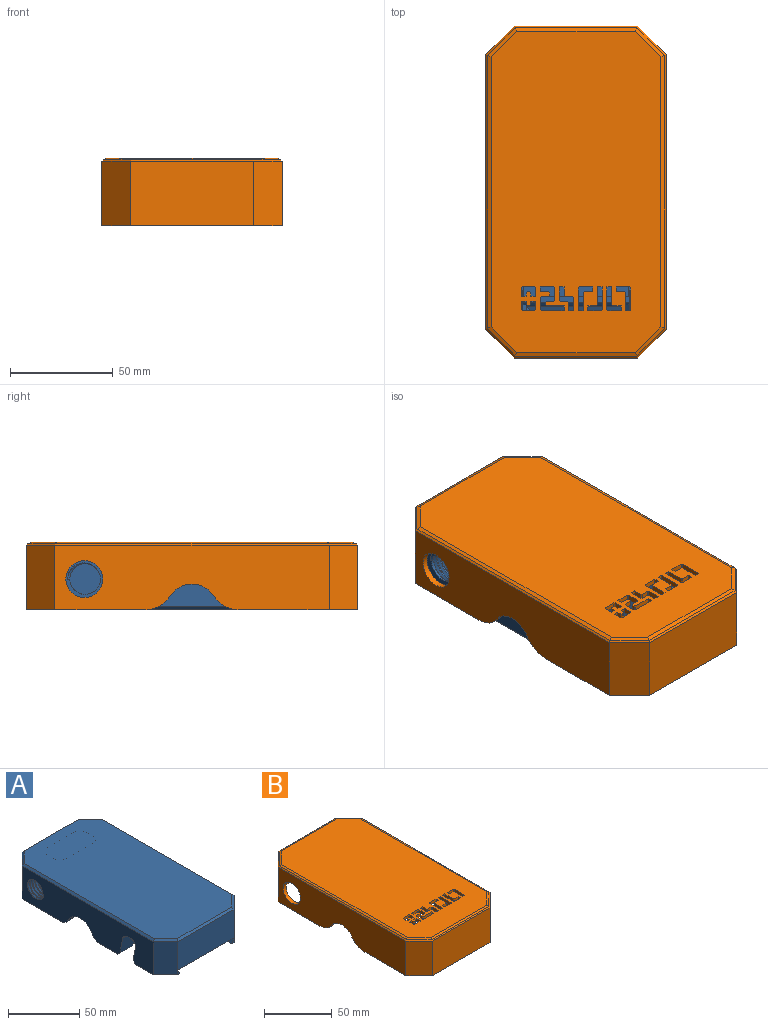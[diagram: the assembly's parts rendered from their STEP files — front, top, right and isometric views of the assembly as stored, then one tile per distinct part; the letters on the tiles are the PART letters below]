
ASSEMBLY  parts=2 mates=3
PART A: 142 faces, bbox 82.7x155.7x31.4 mm
  f0: plane 30x14mm, normal (0,0,-1), area 348mm2, adj f5,f14,f17,f33,f83
  f1: plane 4x2mm, normal (0,-1,0), area 4mm2, adj f13,f34,f82
  f2: plane 56x24.4mm, normal (0,-1,0), area 1366.4mm2, adj f33,f34,f84,f109
  f3: plane 25.83x20.32mm, normal (0,0,-1), area 273.5mm2, adj f4,f14,f15,f26,f67,f71,f85
  f4: plane 14x2.41mm, normal (0,-0.63,-0.77), area 42.1mm2, adj f3,f14,f51,f85
  f5: plane 14x2.94mm, normal (0,0.77,-0.63), area 50.5mm2, adj f0,f14,f52,f83
  f6: plane 53.34x25.97mm, normal (0,0,-1), area 726.6mm2, adj f7,f16,f21,f22,f23,f31,f35,f66
  f7: plane 131.67x29.07mm, normal (-1,0,0), area 3016.5mm2, adj f6,f10,f13,f31,f34,f37,f39,f40
  f8: cone r=37.8mm half-angle=45deg, axis (0,0,-1), area 57mm2, adj f9,f12,f23,f72
  f9: plane 53.34x25.97mm, normal (0,0,-1), area 726.6mm2, adj f8,f14,f16,f21,f23,f24,f32,f68
  f10: plane 25.83x20.32mm, normal (0,0,-1), area 273.5mm2, adj f7,f11,f26,f62,f65,f69,f87
  f11: cone r=37.8mm half-angle=45deg, axis (0,0,-1), area 57mm2, adj f10,f26,f36,f69
  f12: cone r=32.8mm half-angle=22.5deg, axis (0,0,-1), area 726.8mm2, adj f8,f19,f23,f35,f63,f64,f70,f72
  f13: plane 30x14mm, normal (0,0,-1), area 348mm2, adj f1,f7,f34,f61,f82
  f14: plane 131.65x29.05mm, normal (1,0,0), area 3016.5mm2, adj f0,f3,f4,f5,f9,f32,f33,f44
  f15: cone r=37.8mm half-angle=45deg, axis (0,0,-1), area 57mm2, adj f3,f26,f36,f71
  f16: plane 56x28.4mm, normal (0,1,0), area 1418.1mm2, adj f6,f9,f31,f32,f77,f78,f79,f80
  f17: plane 4x2mm, normal (0,-1,0), area 4mm2, adj f0,f33,f83
  f18: plane 151.8x76.8mm, normal (0,0,1), area 11413.5mm2, adj f105,f106,f107,f108,f109,f110,f111,f112
  f19: cylinder r=32.8mm len=65.6mm, axis (0,0,-1), area 2267mm2, adj f12,f30,f36,f63,f64
  f20: plane 60.6x60.6mm, normal (0,0,-1), area 2884.3mm2, adj f30
  f21: plane 51x14.5mm, normal (0,-1,0), area 567.2mm2, adj f6,f9,f22,f24,f25,f77,f78,f79
  f22: plane 31x14.5mm, normal (1,0,0), area 449.5mm2, adj f6,f21,f23,f25
  f23: plane 51.2x14.7mm, normal (0,1,0), area 662.1mm2, adj f6,f8,f9,f12,f22,f24,f25,f35
  f24: plane 31x14.5mm, normal (-1,0,0), area 449.5mm2, adj f9,f21,f23,f25
  f25: plane 51x31mm, normal (0,0,-1), area 458mm2, adj f21,f22,f23,f24,f113,f114,f115,f116
  f26: plane 56.2x27.2mm, normal (0,-1,0), area 1323.1mm2, adj f3,f10,f11,f15,f27,f29,f36,f85
  f27: plane 23x23mm, normal (1,0,0), area 332.7mm2, adj f26,f28,f54,f55,f56,f57,f58,f84
  f28: plane 51.5x23mm, normal (0,1,0), area 1184.5mm2, adj f27,f29,f84,f104
  f29: plane 23x23mm, normal (-1,0,0), area 332.7mm2, adj f26,f28,f51,f52,f53,f59,f60,f84
  f30: cone r=32.8mm half-angle=45deg, axis (0,0,-1), area 700.9mm2, adj f19,f20
  f31: plane 28.4x12mm, normal (-0.71,0.71,0), area 482mm2, adj f6,f7,f16,f106
  f32: plane 28.4x12mm, normal (0.71,0.71,0), area 482mm2, adj f9,f14,f16,f110
  f33: plane 28.4x12mm, normal (0.71,-0.71,0), area 482mm2, adj f0,f2,f14,f17,f111
  f34: plane 28.4x12mm, normal (-0.71,-0.71,0), area 482mm2, adj f1,f2,f7,f13,f107
  f35: cone r=37.8mm half-angle=45deg, axis (0,0,-1), area 57mm2, adj f6,f12,f23,f70
  f36: cone r=32.8mm half-angle=22.5deg, axis (0,0,-1), area 726.8mm2, adj f11,f15,f19,f26,f63,f64,f69,f71
  f37: cylinder r=7.5mm len=15mm, axis (-1,0,0), area 114.4mm2, adj f7,f38,f39,f40,f42,f43
  f38: plane 15x15mm, normal (-1,0,0), area 176.7mm2, adj f37,f41
  f39: plane 1x1mm, normal (0,0,-1), area 0.5mm2, adj f7,f37,f43
  f40: bspline ~19.63x17mm, area 270.1mm2, adj f7,f37,f42,f43
  f41: cylinder r=7.5mm len=13.59mm, axis (1,0,0), area 9.4mm2, adj f38,f42,f43
  f42: plane 2x1mm, normal (0,0,1), area 1mm2, adj f37,f40,f41,f43
  f43: bspline ~19.63x17mm, area 284.7mm2, adj f37,f39,f40,f41,f42
  f44: cylinder r=7.5mm len=15mm, axis (1,0,0), area 114.4mm2, adj f14,f45,f47,f48,f49,f50
  f45: plane 15x15mm, normal (1,0,0), area 176.7mm2, adj f44,f46
  f46: cylinder r=7.5mm len=13.59mm, axis (-1,0,0), area 9.4mm2, adj f45,f48,f49
  f47: plane 1x1mm, normal (0,0,-1), area 0.5mm2, adj f14,f44,f49
  f48: plane 2x1mm, normal (0,0,1), area 1mm2, adj f44,f46,f49,f50
  f49: bspline ~19.63x17mm, area 284.7mm2, adj f44,f46,f47,f48,f50
  f50: bspline ~19.63x17mm, area 270.1mm2, adj f14,f44,f48,f49
  f51: plane 14.25x14mm, normal (0,-0.98,-0.2), area 199.9mm2, adj f4,f14,f29,f59,f85,f86
  f52: plane 14.25x11.08mm, normal (0,0.98,0.2), area 158.8mm2, adj f5,f14,f29,f60,f83,f84
  f53: plane 14.25x2.8mm, normal (0,0,-1), area 39.9mm2, adj f14,f29,f59,f60
  f54: plane 14.25x2.8mm, normal (0,0,-1), area 39.9mm2, adj f7,f27,f57,f58
  f55: plane 14.25x14mm, normal (0,-0.98,-0.2), area 199.9mm2, adj f7,f27,f57,f62,f87,f88
  f56: plane 14.25x11.08mm, normal (0,0.98,0.2), area 158.8mm2, adj f7,f27,f58,f61,f82,f84
  f57: cylinder r=5mm len=14.25mm, axis (-1,0,0), area 97.9mm2, adj f7,f27,f54,f55
  f58: cylinder r=5mm len=14.25mm, axis (-1,0,0), area 126mm2, adj f7,f27,f54,f56
  f59: cylinder r=5mm len=14.25mm, axis (-1,0,0), area 97.9mm2, adj f14,f29,f51,f53
  f60: cylinder r=5mm len=14.25mm, axis (-1,0,0), area 126mm2, adj f14,f29,f52,f53
  f61: plane 14x2.94mm, normal (0,0.77,-0.63), area 50.5mm2, adj f7,f13,f56,f82
  f62: plane 14x2.41mm, normal (0,-0.63,-0.77), area 42.1mm2, adj f7,f10,f55,f87
  f63: cylinder r=12.5mm len=22.56mm, axis (-1,0,0), area 220.3mm2, adj f7,f12,f19,f36,f69,f70,f74,f75
  f64: cylinder r=12.5mm len=22.56mm, axis (-1,0,0), area 220.2mm2, adj f12,f14,f19,f36,f71,f72,f73,f76
  f65: plane 5.16x2.75mm, normal (0,0.6,-0.8), area 16.8mm2, adj f7,f10,f69,f74
  f66: plane 5.16x2.75mm, normal (0,-0.6,-0.8), area 16.8mm2, adj f6,f7,f70,f75
  f67: plane 5.16x2.75mm, normal (0,0.6,-0.8), area 16.8mm2, adj f3,f14,f71,f73
  f68: plane 5.16x2.75mm, normal (0,-0.6,-0.8), area 16.8mm2, adj f9,f14,f72,f76
  f69: bspline ~9.3x8.08mm, area 25.5mm2, adj f10,f11,f36,f63,f65,f74
  f70: bspline ~9.3x8.08mm, area 25.5mm2, adj f6,f12,f35,f63,f66,f75
  f71: bspline ~9.3x8.08mm, area 25.5mm2, adj f3,f15,f36,f64,f67,f73
  f72: bspline ~9.3x8.08mm, area 25.5mm2, adj f8,f9,f12,f64,f68,f76
  f73: plane 6.37x3.46mm, normal (0,0.77,-0.64), area 23.8mm2, adj f14,f64,f67,f71
  f74: plane 6.37x3.46mm, normal (0,0.77,-0.64), area 23.8mm2, adj f7,f63,f65,f69
  f75: plane 6.37x3.46mm, normal (0,-0.77,-0.64), area 23.8mm2, adj f7,f63,f66,f70
  f76: plane 6.37x3.46mm, normal (0,-0.77,-0.64), area 23.8mm2, adj f14,f64,f68,f72
  f77: cylinder r=10mm len=17.38mm, axis (0,1,0), area 84.3mm2, adj f16,f21,f80,f81
  f78: plane 4x2.7mm, normal (0.58,0,-0.82), area 13.2mm2, adj f6,f16,f21,f80
  f79: plane 4x2.7mm, normal (-0.58,0,-0.82), area 13.2mm2, adj f9,f16,f21,f81
  f80: plane 4x3.04mm, normal (0.74,0,-0.67), area 16.4mm2, adj f16,f21,f77,f78
  f81: plane 4x3.04mm, normal (-0.74,0,-0.67), area 16.4mm2, adj f16,f21,f77,f79
  f82: plane 32.41x4mm, normal (0.89,0,0.45), area 140.9mm2, adj f1,f13,f56,f61,f84
  f83: plane 32.41x4mm, normal (-0.89,0,0.45), area 140.9mm2, adj f0,f5,f17,f52,f84
  f84: plane 56x32.2mm, normal (0,0,-1), area 443.4mm2, adj f2,f27,f28,f29,f52,f56,f82,f83
  f85: plane 4.8x4mm, normal (-0.89,0,0.45), area 17.4mm2, adj f3,f4,f26,f51,f86
  f86: plane 4.8x2.25mm, normal (0,0,-1), area 10.8mm2, adj f26,f29,f51,f85
  f87: plane 4.8x4mm, normal (0.89,0,0.45), area 17.4mm2, adj f10,f26,f55,f62,f88
  f88: plane 4.8x2.25mm, normal (0,0,-1), area 10.8mm2, adj f26,f27,f55,f87
  f89: plane 43x12mm, normal (0,0,-1), area 516mm2, adj f90,f91,f92,f93
  f90: plane 48.12x2.56mm, normal (0,0.38,-0.92), area 126.3mm2, adj f89,f92,f93,f94
  f91: plane 48.12x2.56mm, normal (0,-0.38,-0.92), area 126.3mm2, adj f89,f92,f93,f95
  f92: plane 17.12x2.56mm, normal (0.38,0,-0.92), area 40.4mm2, adj f89,f90,f91,f96
  f93: plane 17.12x2.56mm, normal (-0.38,0,-0.92), area 40.4mm2, adj f89,f90,f91,f97
  f94: plane 49.88x0.88mm, normal (0,0.71,-0.71), area 60.9mm2, adj f90,f96,f97,f98
  f95: plane 49.88x0.88mm, normal (0,-0.71,-0.71), area 60.9mm2, adj f91,f96,f97,f99
  f96: plane 19.76x1.94mm, normal (0.71,0,-0.71), area 51.3mm2, adj f92,f94,f95,f98,f99,f103
  f97: plane 19.76x1.94mm, normal (-0.71,0,-0.71), area 51.3mm2, adj f93,f94,f95,f98,f99,f102
  f98: plane 52x2.56mm, normal (0,0.92,-0.38), area 142.9mm2, adj f94,f96,f97,f101,f102,f103
  f99: plane 52x2.56mm, normal (0,-0.92,-0.38), area 142.9mm2, adj f95,f96,f97,f100,f102,f103
  f100: plane 52x18.5mm, normal (0,-1,0), area 962mm2, adj f84,f99,f102,f103
  f101: plane 52x18.5mm, normal (0,1,0), area 962mm2, adj f84,f98,f102,f103
  f102: plane 21x20mm, normal (-1,0,0), area 419.1mm2, adj f84,f97,f98,f99,f100,f101
  f103: plane 21x20mm, normal (1,0,0), area 419.1mm2, adj f84,f96,f98,f99,f100,f101
  f104: plane 51.5x23mm, normal (0,0,-1), area 1184.5mm2, adj f26,f27,f28,f29
  f105: plane 131x1.6mm, normal (-0.71,0,0.71), area 294.9mm2, adj f7,f18,f106,f107
  f106: plane 12.66x12.66mm, normal (-0.5,0.5,0.71), area 36.9mm2, adj f18,f31,f105,f108
  f107: plane 12.66x12.66mm, normal (-0.5,-0.5,0.71), area 36.9mm2, adj f18,f34,f105,f109
  f108: plane 56x1.6mm, normal (0,0.71,0.71), area 125.2mm2, adj f16,f18,f106,f110
  f109: plane 56x1.6mm, normal (0,-0.71,0.71), area 125.2mm2, adj f2,f18,f107,f111
  f110: plane 12.66x12.66mm, normal (0.5,0.5,0.71), area 36.9mm2, adj f18,f32,f108,f112
  f111: plane 12.66x12.66mm, normal (0.5,-0.5,0.71), area 36.9mm2, adj f18,f33,f109,f112
  f112: plane 131x1.6mm, normal (0.71,0,0.71), area 294.9mm2, adj f14,f18,f110,f111
  f113: plane 43x9.68mm, normal (0,1,0), area 416.3mm2, adj f25,f130,f140,f141
  f114: plane 23x9.68mm, normal (1,0,0), area 222.7mm2, adj f25,f135,f139,f140
  f115: plane 43x9.68mm, normal (0,-1,0), area 416.3mm2, adj f25,f137,f138,f139
  f116: plane 23x9.68mm, normal (-1,0,0), area 222.7mm2, adj f25,f134,f138,f141
  f117: plane 39x19mm, normal (0,0,-1), area 706.2mm2, adj f118,f119,f120,f121,f122,f123,f124,f125
  f118: plane 30.7x1.36mm, normal (0,0.71,-0.71), area 56.4mm2, adj f117,f126,f127,f130
  f119: plane 10.7x1.36mm, normal (0.71,0,-0.71), area 18mm2, adj f117,f131,f132,f135
  f120: plane 10.7x1.36mm, normal (-0.71,0,-0.71), area 18mm2, adj f117,f128,f129,f134
  f121: plane 30.7x1.36mm, normal (0,-0.71,-0.71), area 56.4mm2, adj f117,f133,f136,f137
  f122: plane 5.21x5.21mm, normal (-0.41,-0.41,-0.82), area 14.5mm2, adj f117,f128,f133,f134,f137,f138
  f123: plane 5.21x5.21mm, normal (0.41,-0.41,-0.82), area 14.5mm2, adj f117,f132,f135,f136,f137,f139
  f124: plane 5.21x5.21mm, normal (0.41,0.41,-0.82), area 14.5mm2, adj f117,f127,f130,f131,f135,f140
  f125: plane 5.21x5.21mm, normal (-0.41,0.41,-0.82), area 14.5mm2, adj f117,f126,f129,f130,f134,f141
  f126: plane 6.07x3.17mm, normal (-0.21,0.58,-0.79), area 11.4mm2, adj f117,f118,f125,f130
  f127: plane 6.07x3.17mm, normal (0.21,0.58,-0.79), area 11.4mm2, adj f117,f118,f124,f130
  f128: plane 6.07x3.17mm, normal (-0.58,-0.21,-0.79), area 11.4mm2, adj f117,f120,f122,f134
  f129: plane 6.07x3.17mm, normal (-0.58,0.21,-0.79), area 11.4mm2, adj f117,f120,f125,f134
  f130: plane 43.81x3.96mm, normal (0,0.92,-0.38), area 168.5mm2, adj f113,f118,f124,f125,f126,f127,f140,f141
  f131: plane 6.07x3.17mm, normal (0.58,0.21,-0.79), area 11.4mm2, adj f117,f119,f124,f135
  f132: plane 6.07x3.17mm, normal (0.58,-0.21,-0.79), area 11.4mm2, adj f117,f119,f123,f135
  f133: plane 6.07x3.17mm, normal (-0.21,-0.58,-0.79), area 11.4mm2, adj f117,f121,f122,f137
  f134: plane 23.81x3.96mm, normal (-0.92,0,-0.38), area 82.8mm2, adj f116,f120,f122,f125,f128,f129,f138,f141
  f135: plane 23.81x3.96mm, normal (0.92,0,-0.38), area 82.8mm2, adj f114,f119,f123,f124,f131,f132,f139,f140
  f136: plane 6.07x3.17mm, normal (0.21,-0.58,-0.79), area 11.4mm2, adj f117,f121,f123,f137
  f137: plane 43.81x3.96mm, normal (0,-0.92,-0.38), area 168.5mm2, adj f115,f121,f122,f123,f133,f136,f138,f139
  f138: plane 10.66x1mm, normal (-0.71,-0.71,0), area 14.5mm2, adj f25,f115,f116,f122,f134,f137
  f139: plane 10.66x1mm, normal (0.71,-0.71,0), area 14.5mm2, adj f25,f114,f115,f123,f135,f137
  f140: plane 10.66x1mm, normal (0.71,0.71,0), area 14.5mm2, adj f25,f113,f114,f124,f130,f135
  f141: plane 10.66x1mm, normal (-0.71,0.71,0), area 14.5mm2, adj f25,f113,f116,f125,f130,f134
PART B: 132 faces, bbox 88x161.8x33 mm
  f0: plane 156.6x82.8mm, normal (0,0,1), area 12343mm2, adj f36,f37,f38,f39,f40,f41,f42,f43
  f1: plane 133.8x31.4mm, normal (1,0,0), area 3669.4mm2, adj f2,f6,f17,f18,f20,f22,f24,f25
  f2: plane 88x57.85mm, normal (0,0,-1), area 541.1mm2, adj f1,f3,f5,f7,f9,f10,f12,f13
  f3: plane 133.8x31.4mm, normal (-1,0,0), area 3669.4mm2, adj f2,f6,f16,f19,f21,f23,f26,f27
  f4: plane 60x31.4mm, normal (0,-1,0), area 1884mm2, adj f6,f18,f19,f31
  f5: plane 60x31.4mm, normal (0,1,0), area 1884mm2, adj f2,f16,f17,f32
  f6: plane 88x57.85mm, normal (0,0,-1), area 541.1mm2, adj f1,f3,f4,f7,f8,f9,f14,f15
  f7: plane 131.8x30.4mm, normal (1,0,0), area 3474.8mm2, adj f2,f6,f11,f12,f15,f21,f23,f26
  f8: plane 58x30.4mm, normal (0,1,0), area 1763.2mm2, adj f6,f11,f14,f15
  f9: plane 131.8x30.4mm, normal (-1,0,0), area 3474.8mm2, adj f2,f6,f11,f13,f14,f20,f22,f24
  f10: plane 58x30.4mm, normal (0,-1,0), area 1763.2mm2, adj f2,f11,f12,f13
  f11: plane 155.8x82mm, normal (0,0,-1), area 12175.4mm2, adj f7,f8,f9,f10,f12,f13,f14,f15
  f12: plane 30.4x12mm, normal (0.71,-0.71,0), area 515.9mm2, adj f2,f7,f10,f11
  f13: plane 30.4x12mm, normal (-0.71,-0.71,0), area 515.9mm2, adj f2,f9,f10,f11
  f14: plane 30.4x12mm, normal (-0.71,0.71,0), area 515.9mm2, adj f6,f8,f9,f11
  f15: plane 30.4x12mm, normal (0.71,0.71,0), area 515.9mm2, adj f6,f7,f8,f11
  f16: plane 31.4x14mm, normal (-0.71,0.71,0), area 621.7mm2, adj f2,f3,f5,f30
  f17: plane 31.4x14mm, normal (0.71,0.71,0), area 621.7mm2, adj f1,f2,f5,f34
  f18: plane 31.4x14mm, normal (0.71,-0.71,0), area 621.7mm2, adj f1,f4,f6,f33
  f19: plane 31.4x14mm, normal (-0.71,-0.71,0), area 621.7mm2, adj f3,f4,f6,f29
  f20: cylinder r=9mm len=18mm, axis (-1,0,0), area 169.6mm2, adj f1,f9
  f21: cylinder r=9mm len=18mm, axis (-1,0,0), area 169.6mm2, adj f3,f7
  f22: cylinder r=12.5mm len=20.95mm, axis (1,0,0), area 74.5mm2, adj f1,f9,f24,f25
  f23: cylinder r=12.5mm len=20.95mm, axis (1,0,0), area 74.5mm2, adj f3,f7,f26,f27
  f24: cylinder r=15mm len=12.57mm, axis (1,0,0), area 44.7mm2, adj f1,f6,f9,f22
  f25: cylinder r=15mm len=12.57mm, axis (1,0,0), area 44.7mm2, adj f1,f2,f9,f22
  f26: cylinder r=15mm len=12.57mm, axis (1,0,0), area 44.7mm2, adj f2,f3,f7,f23
  f27: cylinder r=15mm len=12.57mm, axis (1,0,0), area 44.7mm2, adj f3,f6,f7,f23
  f28: plane 133.8x0.89mm, normal (-0.71,0,0.71), area 168.5mm2, adj f3,f29,f30,f36
  f29: plane 14.37x14.37mm, normal (-0.5,-0.5,0.71), area 24.5mm2, adj f19,f28,f31,f37
  f30: plane 14.37x14.37mm, normal (-0.5,0.5,0.71), area 24.5mm2, adj f16,f28,f32,f38
  f31: plane 60x0.89mm, normal (0,-0.71,0.71), area 75.3mm2, adj f4,f29,f33,f39
  f32: plane 60x0.89mm, normal (0,0.71,0.71), area 75.3mm2, adj f5,f30,f34,f40
  f33: plane 14.37x14.37mm, normal (0.5,-0.5,0.71), area 24.5mm2, adj f18,f31,f35,f41
  f34: plane 14.37x14.37mm, normal (0.5,0.5,0.71), area 24.5mm2, adj f17,f32,f35,f42
  f35: plane 133.8x0.89mm, normal (0.71,0,0.71), area 168.5mm2, adj f1,f33,f34,f43
  f36: plane 133.06x1.71mm, normal (-0.38,0,0.92), area 244.6mm2, adj f0,f28,f37,f38
  f37: plane 14.18x14.18mm, normal (-0.27,-0.27,0.92), area 33.9mm2, adj f0,f29,f36,f39
  f38: plane 14.18x14.18mm, normal (-0.27,0.27,0.92), area 33.9mm2, adj f0,f30,f36,f40
  f39: plane 59.26x1.71mm, normal (0,-0.38,0.92), area 108.2mm2, adj f0,f31,f37,f41
  f40: plane 59.26x1.71mm, normal (0,0.38,0.92), area 108.2mm2, adj f0,f32,f38,f42
  f41: plane 14.18x14.18mm, normal (0.27,-0.27,0.92), area 33.9mm2, adj f0,f33,f39,f43
  f42: plane 14.18x14.18mm, normal (0.27,0.27,0.92), area 33.9mm2, adj f0,f34,f40,f43
  f43: plane 133.06x1.71mm, normal (0.38,0,0.92), area 244.6mm2, adj f0,f35,f41,f42
  f44: plane 4.14x2.6mm, normal (0,1,0), area 10.8mm2, adj f0,f11,f45,f125
  f45: plane 2.6x2.32mm, normal (1,0,0), area 6mm2, adj f0,f11,f44,f46
  f46: plane 6.46x2.6mm, normal (0,-1,0), area 16.8mm2, adj f0,f11,f45,f124
  f47: plane 11.1x2.6mm, normal (-1,0,0), area 28.9mm2, adj f0,f11,f48,f124
  f48: plane 2.6x2.32mm, normal (0,1,0), area 6mm2, adj f0,f11,f47,f49
  f49: plane 8.78x2.6mm, normal (1,0,0), area 22.8mm2, adj f0,f11,f48,f125
  f50: plane 11.1x2.6mm, normal (0,1,0), area 28.9mm2, adj f0,f11,f61,f112
  f51: plane 5.96x2.6mm, normal (1,0,0), area 15.5mm2, adj f0,f11,f112,f118
  f52: plane 3.64x2.6mm, normal (0,-1,0), area 9.5mm2, adj f0,f11,f117,f118
  f53: plane 2.6x1.32mm, normal (1,0,0), area 3.4mm2, adj f0,f11,f116,f117
  f54: plane 4.14x2.6mm, normal (0,1,0), area 10.8mm2, adj f0,f11,f55,f116
  f55: plane 2.6x2.32mm, normal (1,0,0), area 6mm2, adj f0,f11,f54,f56
  f56: plane 6.46x2.6mm, normal (0,-1,0), area 16.8mm2, adj f0,f11,f55,f115
  f57: plane 5.96x2.6mm, normal (-1,0,0), area 15.5mm2, adj f0,f11,f115,f119
  f58: plane 3.64x2.6mm, normal (0,1,0), area 9.5mm2, adj f0,f11,f113,f119
  f59: plane 2.6x1.32mm, normal (-1,0,0), area 3.4mm2, adj f0,f11,f113,f114
  f60: plane 8.78x2.6mm, normal (0,-1,0), area 22.8mm2, adj f0,f11,f61,f114
  f61: plane 2.6x2.32mm, normal (-1,0,0), area 6mm2, adj f0,f11,f50,f60
  f62: plane 4.14x2.6mm, normal (-1,0,0), area 10.8mm2, adj f0,f11,f63,f108
  f63: plane 2.6x2.32mm, normal (0,1,0), area 6mm2, adj f0,f11,f62,f64
  f64: plane 2.6x1.82mm, normal (1,0,0), area 4.7mm2, adj f0,f11,f63,f105
  f65: plane 2.6x1.32mm, normal (0,1,0), area 3.4mm2, adj f0,f11,f104,f105
  f66: plane 2.6x1.82mm, normal (-1,0,0), area 4.7mm2, adj f0,f11,f67,f104
  f67: plane 2.6x2.32mm, normal (0,1,0), area 6mm2, adj f0,f11,f66,f68
  f68: plane 4.14x2.6mm, normal (1,0,0), area 10.8mm2, adj f0,f11,f67,f109
  f69: plane 5.96x2.6mm, normal (0,-1,0), area 15.5mm2, adj f0,f11,f108,f109
  f70: plane 4.14x2.6mm, normal (-1,0,0), area 10.8mm2, adj f0,f11,f77,f111
  f71: plane 5.96x2.6mm, normal (0,1,0), area 15.5mm2, adj f0,f11,f110,f111
  f72: plane 4.14x2.6mm, normal (1,0,0), area 10.8mm2, adj f0,f11,f73,f110
  f73: plane 2.6x2.32mm, normal (0,-1,0), area 6mm2, adj f0,f11,f72,f74
  f74: plane 2.6x1.82mm, normal (-1,0,0), area 4.7mm2, adj f0,f11,f73,f106
  f75: plane 2.6x1.32mm, normal (0,-1,0), area 3.4mm2, adj f0,f11,f106,f107
  f76: plane 2.6x1.82mm, normal (1,0,0), area 4.7mm2, adj f0,f11,f77,f107
  f77: plane 2.6x2.32mm, normal (0,-1,0), area 6mm2, adj f0,f11,f70,f76
  f78: plane 8.78x2.6mm, normal (-1,0,0), area 22.8mm2, adj f0,f11,f83,f126
  f79: plane 4.14x2.6mm, normal (0,-1,0), area 10.8mm2, adj f0,f11,f80,f126
  f80: plane 2.6x2.32mm, normal (-1,0,0), area 6mm2, adj f0,f11,f79,f81
  f81: plane 6.46x2.6mm, normal (0,1,0), area 16.8mm2, adj f0,f11,f80,f127
  f82: plane 11.1x2.6mm, normal (1,0,0), area 28.9mm2, adj f0,f11,f83,f127
  f83: plane 2.6x2.32mm, normal (0,-1,0), area 6mm2, adj f0,f11,f78,f82
  f84: plane 6.46x2.6mm, normal (0,1,0), area 16.8mm2, adj f0,f11,f85,f128
  f85: plane 2.6x2.32mm, normal (1,0,0), area 6mm2, adj f0,f11,f84,f86
  f86: plane 4.14x2.6mm, normal (0,-1,0), area 10.8mm2, adj f0,f11,f85,f129
  f87: plane 8.78x2.6mm, normal (1,0,0), area 22.8mm2, adj f0,f11,f88,f129
  f88: plane 2.6x2.32mm, normal (0,-1,0), area 6mm2, adj f0,f11,f87,f89
  f89: plane 11.1x2.6mm, normal (-1,0,0), area 28.9mm2, adj f0,f11,f88,f128
  f90: plane 4.14x2.6mm, normal (0,1,0), area 10.8mm2, adj f0,f11,f95,f131
  f91: plane 8.78x2.6mm, normal (-1,0,0), area 22.8mm2, adj f0,f11,f92,f131
  f92: plane 2.6x2.32mm, normal (0,1,0), area 6mm2, adj f0,f11,f91,f93
  f93: plane 11.1x2.6mm, normal (1,0,0), area 28.9mm2, adj f0,f11,f92,f130
  f94: plane 6.46x2.6mm, normal (0,-1,0), area 16.8mm2, adj f0,f11,f95,f130
  f95: plane 2.6x2.32mm, normal (-1,0,0), area 6mm2, adj f0,f11,f90,f94
  f96: plane 2.6x2.32mm, normal (0,1,0), area 6mm2, adj f0,f11,f97,f103
  f97: plane 4.14x2.6mm, normal (1,0,0), area 10.8mm2, adj f0,f11,f96,f122
  f98: plane 3.64x2.6mm, normal (0,1,0), area 9.5mm2, adj f0,f11,f121,f122
  f99: plane 6.46x2.6mm, normal (1,0,0), area 16.8mm2, adj f0,f11,f100,f121
  f100: plane 2.6x2.32mm, normal (0,-1,0), area 6mm2, adj f0,f11,f99,f101
  f101: plane 4.14x2.6mm, normal (-1,0,0), area 10.8mm2, adj f0,f11,f100,f123
  f102: plane 3.64x2.6mm, normal (0,-1,0), area 9.5mm2, adj f0,f11,f120,f123
  f103: plane 6.46x2.6mm, normal (-1,0,0), area 16.8mm2, adj f0,f11,f96,f120
  f104: plane 2.6x0.5mm, normal (-0.71,0.71,0), area 1.8mm2, adj f0,f11,f65,f66
  f105: plane 2.6x0.5mm, normal (0.71,0.71,0), area 1.8mm2, adj f0,f11,f64,f65
  f106: plane 2.6x0.5mm, normal (-0.71,-0.71,0), area 1.8mm2, adj f0,f11,f74,f75
  f107: plane 2.6x0.5mm, normal (0.71,-0.71,0), area 1.8mm2, adj f0,f11,f75,f76
  f108: plane 2.6x0.5mm, normal (-0.71,-0.71,0), area 1.8mm2, adj f0,f11,f62,f69
  f109: plane 2.6x0.5mm, normal (0.71,-0.71,0), area 1.8mm2, adj f0,f11,f68,f69
  f110: plane 2.6x0.5mm, normal (0.71,0.71,0), area 1.8mm2, adj f0,f11,f71,f72
  f111: plane 2.6x0.5mm, normal (-0.71,0.71,0), area 1.8mm2, adj f0,f11,f70,f71
  f112: plane 2.6x0.5mm, normal (0.71,0.71,0), area 1.8mm2, adj f0,f11,f50,f51
  f113: plane 2.6x0.5mm, normal (-0.71,0.71,0), area 1.8mm2, adj f0,f11,f58,f59
  f114: plane 2.6x0.5mm, normal (-0.71,-0.71,0), area 1.8mm2, adj f0,f11,f59,f60
  f115: plane 2.6x0.5mm, normal (-0.71,-0.71,0), area 1.8mm2, adj f0,f11,f56,f57
  f116: plane 2.6x0.5mm, normal (0.71,0.71,0), area 1.8mm2, adj f0,f11,f53,f54
  f117: plane 2.6x0.5mm, normal (0.71,-0.71,0), area 1.8mm2, adj f0,f11,f52,f53
  f118: plane 2.6x0.5mm, normal (0.71,-0.71,0), area 1.8mm2, adj f0,f11,f51,f52
  f119: plane 2.6x0.5mm, normal (-0.71,0.71,0), area 1.8mm2, adj f0,f11,f57,f58
  f120: plane 2.6x0.5mm, normal (-0.71,-0.71,0), area 1.8mm2, adj f0,f11,f102,f103
  f121: plane 2.6x0.5mm, normal (0.71,0.71,0), area 1.8mm2, adj f0,f11,f98,f99
  f122: plane 2.6x0.5mm, normal (0.71,0.71,0), area 1.8mm2, adj f0,f11,f97,f98
  f123: plane 2.6x0.5mm, normal (-0.71,-0.71,0), area 1.8mm2, adj f0,f11,f101,f102
  f124: plane 2.6x0.5mm, normal (-0.71,-0.71,0), area 1.8mm2, adj f0,f11,f46,f47
  f125: plane 2.6x0.5mm, normal (0.71,0.71,0), area 1.8mm2, adj f0,f11,f44,f49
  f126: plane 2.6x0.5mm, normal (-0.71,-0.71,0), area 1.8mm2, adj f0,f11,f78,f79
  f127: plane 2.6x0.5mm, normal (0.71,0.71,0), area 1.8mm2, adj f0,f11,f81,f82
  f128: plane 2.6x0.5mm, normal (-0.71,0.71,0), area 1.8mm2, adj f0,f11,f84,f89
  f129: plane 2.6x0.5mm, normal (0.71,-0.71,0), area 1.8mm2, adj f0,f11,f86,f87
  f130: plane 2.6x0.5mm, normal (0.71,-0.71,0), area 1.8mm2, adj f0,f11,f93,f94
  f131: plane 2.6x0.5mm, normal (-0.71,0.71,0), area 1.8mm2, adj f0,f11,f90,f91
PLACE A rot(axis=(0,1,0),180deg) t=(84.87,12.98,18.1)mm fixed
PLACE B t=(-16.13,13.38,-11.9)mm
MATE parallel A.f0 <-> B.f6  axis (0,0,1) through (52.49,-54.74,18.1)mm
MATE parallel A.f2 <-> B.f8  axis (0,-1,0) through (84.87,-72.02,14.1)mm
MATE parallel A.f7 <-> B.f9  axis (1,0,0) through (124.87,-60.02,3.9)mm
